# Revit family: Faucet-Deck_Mount-Bath-KOHLER-FINIAL-K-8673T
name_source: partatom
category: Plumbing Fixtures
revit_build: Autodesk Revit 2017 (Build: 20160225_1515(x64)
units: mm (PartAtom-declared; Revit-internal decimal feet)

## family parameters
Cut with Voids When Loaded = No
Host = Face
OmniClass Number = 23.31.11.00
OmniClass Title = Faucets
Part Type = Normal
Room Calculation Point = No
Round Connector Dimension = Use Diameter
Shared = No

## types (5) — shared parameters
ADA Compliant = No
Assembly Code = D2010
CW Connection = Yes
Cold Water Inlet = Cold Water Inlet
Date Modified = 09/28/2020
Default Elevation = 36"
Description = TRADITIONAL DECKMOUNT FAUCET
Drain Included = No
Flow Rate = 0 GPM
HW Connection = Yes
Handle Clearance = 3 13/16"
Height = 9 13/16"
Hot Water Inlet = Hot Water Inlet
Length = 7 1/2"
Manufacturer = KOHLER Co.
Master Format 2014 = 22 41 39
Master Format 2014 Name = Residential Faucets, Supplies, and Trim
Material = Metal construction
Pressure = 0.00 psi
Product Documentation Link = https://files.kohler.com.cn
Product Name = FINIAL
Product Page URL = https://www.kohler.com.cn
Spout Reach = 7 1/2"
URL = http://www.kohler.com.cn
Vent Connection = No
Waste Connection = No
Waste Water Outlet = Waste Water Outlet
WaterSense Certified = No

## per-type parameters (varying)
| type | Finish | Handle finish | Model | Type |
| CP- Polished chrome | Kohler-Metal-CP-Polished_Chrome | Kohler-Metal-CP-Polished_Chrome | K-8673T-4M-CP | 1 |
| Lever Handles With White Accents,CP- Polished chrome | Kohler-Metal-CP-Polished_Chrome | Kohler-Plastic-0-White | K-8673T-4P-CP | 5 |
| AF- French gold | Kohler-Metal-AF-Vibrant_French_Gold | Kohler-Metal-AF-Vibrant_French_Gold | K-8673T-4M-AF | 2 |
| SN- Polished nickel | Kohler-Metal-SN-Vibrant_Polished_Nickel | Kohler-Metal-SN-Vibrant_Polished_Nickel | K-8673T-4M-SN | 3 |
| BN- Brushed nickel | Kohler-Metal-BN-Vibrant_Brushed_Nickel | Kohler-Metal-BN-Vibrant_Brushed_Nickel | K-8673T-4M-BN | 4 |

## geometry (parser evidence)
native form markers: Sweep x7
no freeform markers — native parametric forms only
